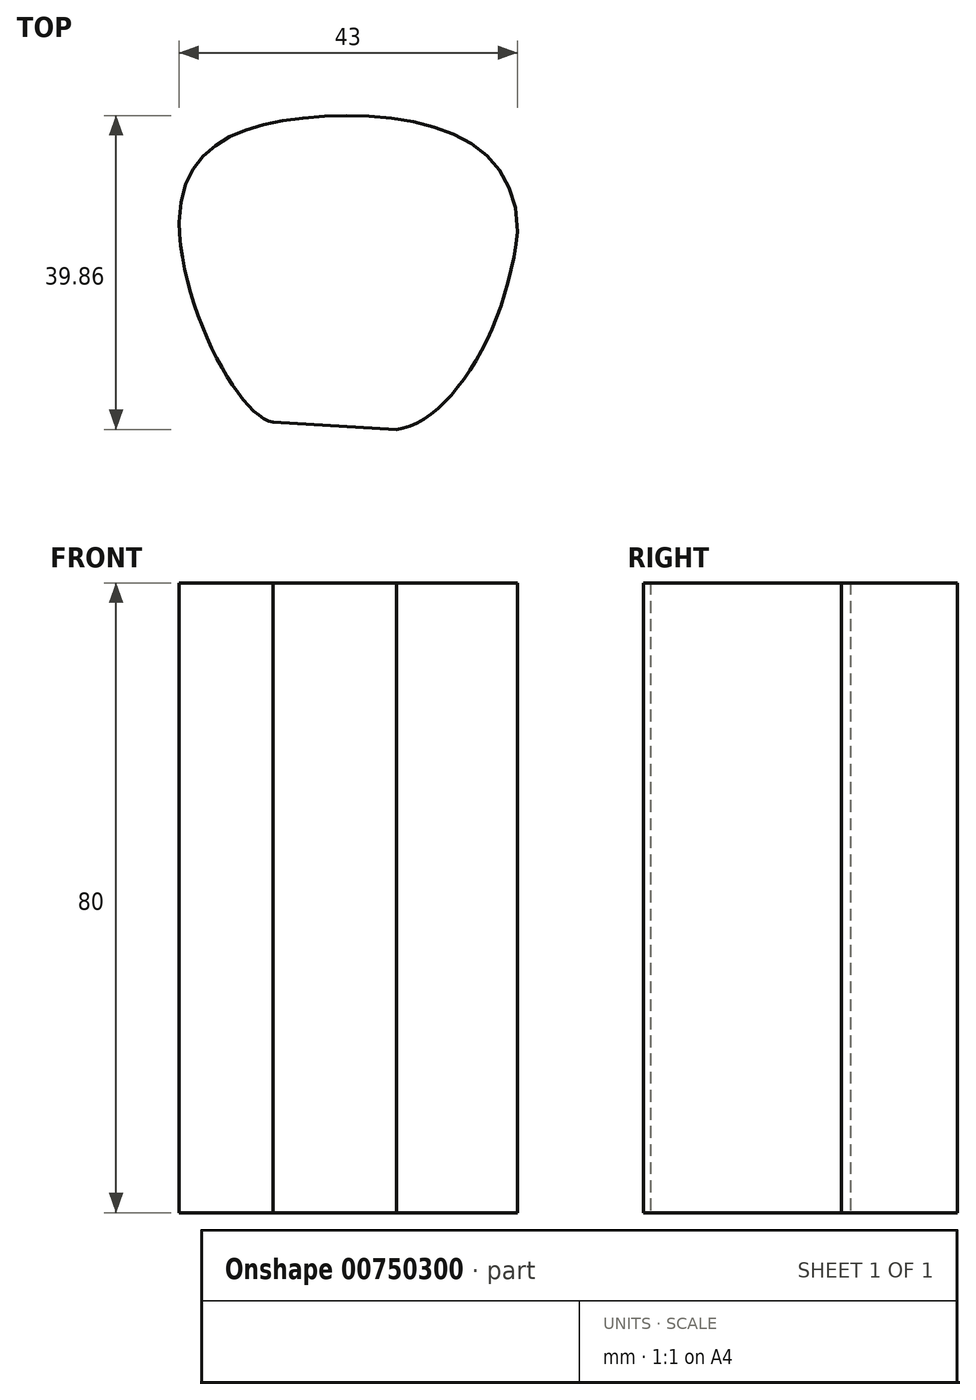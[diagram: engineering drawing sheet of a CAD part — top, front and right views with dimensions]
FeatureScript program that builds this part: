
annotation { "Feature Type Name" : "Feature", "Feature Type Description" : "" }
export const myFeature = defineFeature(function(context is Context, id is Id, definition is map)
    precondition{}
    {
        {
            var Q0;
            Q0=qCreatedBy(makeId("Top.planeOp"),FACE);
            var sketch = newSketch(context, id + "F0", { "sketchPlane" : qUnion([Q0])});
            skLineSegment(sketch, "E0", {"start": v(-20.96, -0.33) * mm, "end": v(-36.62, 0.59) * mm});
            skFitSpline(sketch, "E1", {"points": [v(-20.96, -0.33) * mm, v(-5.56, 24.83) * mm], "startDerivative": vector(20.27, 2.24) * mm, "endDerivative": vector(3.83, 37.7) * mm});
            skFitSpline(sketch, "E2", {"points": [v(-5.56, 24.83) * mm, v(-30.9, 39.4) * mm, v(-48.56, 25.99) * mm], "startDerivative": vector(-0.1, 73.75) * mm, "endDerivative": vector(-1.21, -63.56) * mm});
            skFitSpline(sketch, "E3", {"points": [v(-48.56, 25.99) * mm, v(-36.62, 0.59) * mm], "startDerivative": vector(0.63, -33.41) * mm, "endDerivative": vector(12.59, -1.95) * mm});
            skSolve(sketch);
        }
        {
            var Q0;
            Q0 = qSketchRegion(id + "F0", true);
            extrude(context, id + "F1", {"entities" : qUnion([Q0]), "endBound" : BoundingType.SYMMETRIC, "depth" : 80 * mm, "offsetDistance" : 25 * mm});
        }
    });
